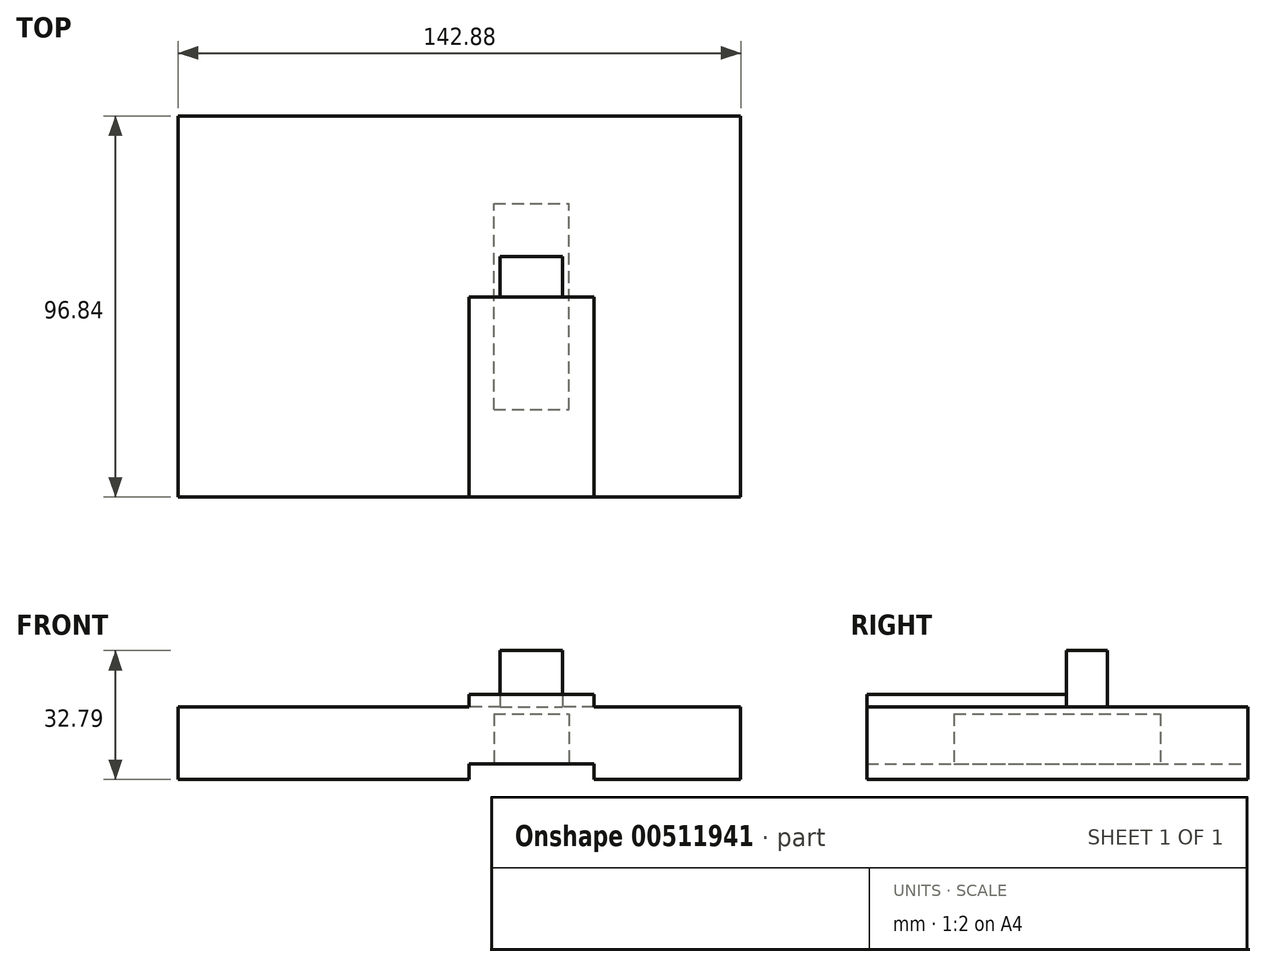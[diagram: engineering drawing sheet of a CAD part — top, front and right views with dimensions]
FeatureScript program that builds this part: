
annotation { "Feature Type Name" : "Feature", "Feature Type Description" : "" }
export const myFeature = defineFeature(function(context is Context, id is Id, definition is map)
    precondition{}
    {
        {
            var Q0;
            Q0=qCreatedBy(makeId("Right.planeOp"),FACE);
            var sketch = newSketch(context, id + "F0", { "sketchPlane" : qUnion([Q0])});
            skLineSegment(sketch, "E0.bottom", {"start": v(-48.42, 15.27) * mm, "end": v(48.42, 15.27) * mm});
            skLineSegment(sketch, "E0.top", {"start": v(-48.42, -3.23) * mm, "end": v(48.42, -3.23) * mm});
            skLineSegment(sketch, "E0.left", {"start": v(-48.42, 15.27) * mm, "end": v(-48.42, -3.23) * mm});
            skLineSegment(sketch, "E0.right", {"start": v(48.42, 15.27) * mm, "end": v(48.42, -3.23) * mm});
            skSolve(sketch);
        }
        {
            var Q0;
            Q0=makeQuery(id+"F0.imprint","IMPRINT",FACE,{"disambiguationData":[TD([[makeQuery(id+"F0.imprint","IMPRINT",EDGE,{"derivedFrom":sQuery(id+"F0.wireOp",EDGE,"E0.bottom")}),-1.0]])]});
            extrude(context, id + "F1", {"entities" : qUnion([Q0]), "depth" : 142.88 * mm, "offsetDistance" : 25.4 * mm});
        }
        {
            var Q0;
            Q0=makeQuery(id+"F1.opExtrude","SWEPT_FACE",FACE,{"disambiguationData":[OSD([sQuery(id+"F0.wireOp",EDGE,"E0.bottom")])]});
            var sketch = newSketch(context, id + "F2", { "sketchPlane" : qUnion([Q0])});
            skLineSegment(sketch, "E1.bottom", {"start": v(105.57, -48.42) * mm, "end": v(73.82, -48.42) * mm});
            skLineSegment(sketch, "E1.top", {"start": v(105.57, 2.38) * mm, "end": v(73.82, 2.38) * mm});
            skLineSegment(sketch, "E1.left", {"start": v(105.57, -48.42) * mm, "end": v(105.57, 2.38) * mm});
            skLineSegment(sketch, "E1.right", {"start": v(73.82, -48.42) * mm, "end": v(73.82, 2.38) * mm});
            skSolve(sketch);
        }
        {
            var Q0;
            Q0 = qSketchRegion(id + "F2", true);
            extrude(context, id + "F3", {"entities" : qUnion([Q0]), "operationType" : NewBodyOperationType.ADD, "depth" : 3.17 * mm, "offsetDistance" : 25.4 * mm});
        }
        {
            var Q0;
            Q0=makeQuery(id+"F1.opExtrude","SWEPT_FACE",FACE,{"disambiguationData":[OSD([sQuery(id+"F0.wireOp",EDGE,"E0.bottom")])]});
            var sketch = newSketch(context, id + "F4", { "sketchPlane" : qUnion([Q0])});
            skLineSegment(sketch, "E2.bottom", {"start": v(81.76, 12.7) * mm, "end": v(97.63, 12.7) * mm});
            skLineSegment(sketch, "E2.top", {"start": v(81.76, -12.7) * mm, "end": v(97.63, -12.7) * mm});
            skLineSegment(sketch, "E2.left", {"start": v(81.76, 12.7) * mm, "end": v(81.76, -12.7) * mm});
            skLineSegment(sketch, "E2.right", {"start": v(97.63, 12.7) * mm, "end": v(97.63, -12.7) * mm});
            skLineSegment(sketch, "E3", {"start": v(89.7, -15.76) * mm, "end": v(89.7, 13) * mm, "construction": true});
            skPoint(sketch, "E3.startSnap0", {"position": v(89.7, -12.7) * mm});
            skSolve(sketch);
        }
        {
            var Q0;
            Q0=makeQuery(id+"F4.imprint","IMPRINT",FACE,{"disambiguationData":[TD([[makeQuery(id+"F4.imprint","IMPRINT",EDGE,{"derivedFrom":sQuery(id+"F4.wireOp",EDGE,"E2.bottom")}),-1.0]])]});
            extrude(context, id + "F5", {"entities" : qUnion([Q0]), "operationType" : NewBodyOperationType.ADD, "depth" : 14.29 * mm, "offsetDistance" : 25.4 * mm});
        }
        {
            var Q0;
            Q0=makeQuery(id+"F1.opExtrude","SWEPT_FACE",FACE,{"disambiguationData":[OSD([sQuery(id+"F0.wireOp",EDGE,"E0.top")])]});
            var sketch = newSketch(context, id + "F6", { "sketchPlane" : qUnion([Q0])});
            skLineSegment(sketch, "E4.0", {"start": v(73.82, 48.42) * mm, "end": v(73.82, 27.78) * mm});
            skLineSegment(sketch, "E5.0", {"start": v(105.57, 48.42) * mm, "end": v(105.57, 27.78) * mm});
            skLineSegment(sketch, "E6", {"start": v(73.82, 27.78) * mm, "end": v(73.82, -48.42) * mm});
            skLineSegment(sketch, "E7", {"start": v(105.57, 27.78) * mm, "end": v(105.57, -48.42) * mm});
            skLineSegment(sketch, "E8.bottom", {"start": v(73.82, 48.42) * mm, "end": v(105.57, 48.42) * mm});
            skLineSegment(sketch, "E8.top", {"start": v(73.82, -48.42) * mm, "end": v(105.57, -48.42) * mm});
            skLineSegment(sketch, "E8.left", {"start": v(73.82, 48.42) * mm, "end": v(73.82, -48.42) * mm});
            skLineSegment(sketch, "E8.right", {"start": v(105.57, 48.42) * mm, "end": v(105.57, -48.42) * mm});
            skSolve(sketch);
        }
        {
            var Q0;
            Q0=makeQuery(id+"F6.imprint","IMPRINT",FACE,{"disambiguationData":[TD([[makeQuery(id+"F6.imprint","IMPRINT",EDGE,{"derivedFrom":sQuery(id+"F6.wireOp",EDGE,"E8.bottom")}),1.0]])]});
            extrude(context, id + "F7", {"entities" : qUnion([Q0]), "operationType" : NewBodyOperationType.REMOVE, "oppositeDirection" : true, "depth" : 3.97 * mm, "offsetDistance" : 25.4 * mm});
        }
        {
            var Q0;
            Q0=makeQuery(id+"F7.boolean.opBoolean","COPY",FACE,{"derivedFrom":makeQuery(id+"F7.opExtrude","CAP_FACE",FACE,{"disambiguationData":[OSD([sQuery(id+"F6.wireOp",EDGE,"E8.bottom"),sQuery(id+"F6.wireOp",EDGE,"E8.top"),sQuery(id+"F6.wireOp",EDGE,"E8.left"),sQuery(id+"F6.wireOp",EDGE,"E8.right")])],"isStart":false})});
            var sketch = newSketch(context, id + "F8", { "sketchPlane" : qUnion([Q0])});
            skLineSegment(sketch, "E9.bottom", {"start": v(80.17, 26.2) * mm, "end": v(99.22, 26.2) * mm});
            skLineSegment(sketch, "E9.top", {"start": v(80.17, -26.2) * mm, "end": v(99.22, -26.2) * mm});
            skLineSegment(sketch, "E9.left", {"start": v(80.17, 26.2) * mm, "end": v(80.17, -26.2) * mm});
            skLineSegment(sketch, "E9.right", {"start": v(99.22, 26.2) * mm, "end": v(99.22, -26.2) * mm});
            skLineSegment(sketch, "E10", {"start": v(89.7, -48.42) * mm, "end": v(89.7, 48.42) * mm, "construction": true});
            skSolve(sketch);
        }
        {
            var Q0;
            Q0=makeQuery(id+"F8.imprint","IMPRINT",FACE,{"disambiguationData":[TD([[makeQuery(id+"F8.imprint","IMPRINT",EDGE,{"derivedFrom":sQuery(id+"F8.wireOp",EDGE,"E9.bottom")}),-1.0]])]});
            extrude(context, id + "F9", {"entities" : qUnion([Q0]), "operationType" : NewBodyOperationType.REMOVE, "oppositeDirection" : true, "depth" : 12.7 * mm, "offsetDistance" : 25.4 * mm});
        }
    });
